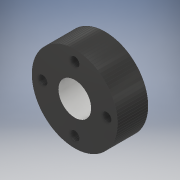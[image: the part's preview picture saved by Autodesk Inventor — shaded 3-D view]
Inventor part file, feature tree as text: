
AUTODESK INVENTOR PART (.ipt)
format: ipt  version: 2019 (Build 230136000, 136)  size: 1,561,088 bytes
history: native  units: in
note: dims shown in document units (in); Inventor stores cm internally (conversion verified against a paired STEP export)
features: other x6, direct_edit x2, plane x2, surface_op x1, extrude x1, sketch x1
ambient origin geometry x8: Origin, YZ Plane, XZ Plane, XY Plane, X Axis, Y Axis, Z Axis, Center Point
bodies: Solid1 (feature_tree)
feature tree (13):
  other  "shoulder_spacer"
  surface_op  "Stitch Surface1"
  direct_edit  "Direct Edit1"
  direct_edit  "Direct Edit2"
  plane  "Work Plane3"
  other  "Work Axis2"
  extrude  "Extrusion1"  Depth=0.3937in
  plane  "Work Plane4"
  sketch  "Sketch1"  dims[d0=0.0394in d1=0.3937in d2=0.3937in d3=0.1606in d4=0.3937in d5=0.3937in d6=90.0deg d7=0.4409in d8=0.3937in d9=0.0in]
  other  "Composite1"
  other  "Srf1"
  other  "Scale1"
  other  "Scale2"
